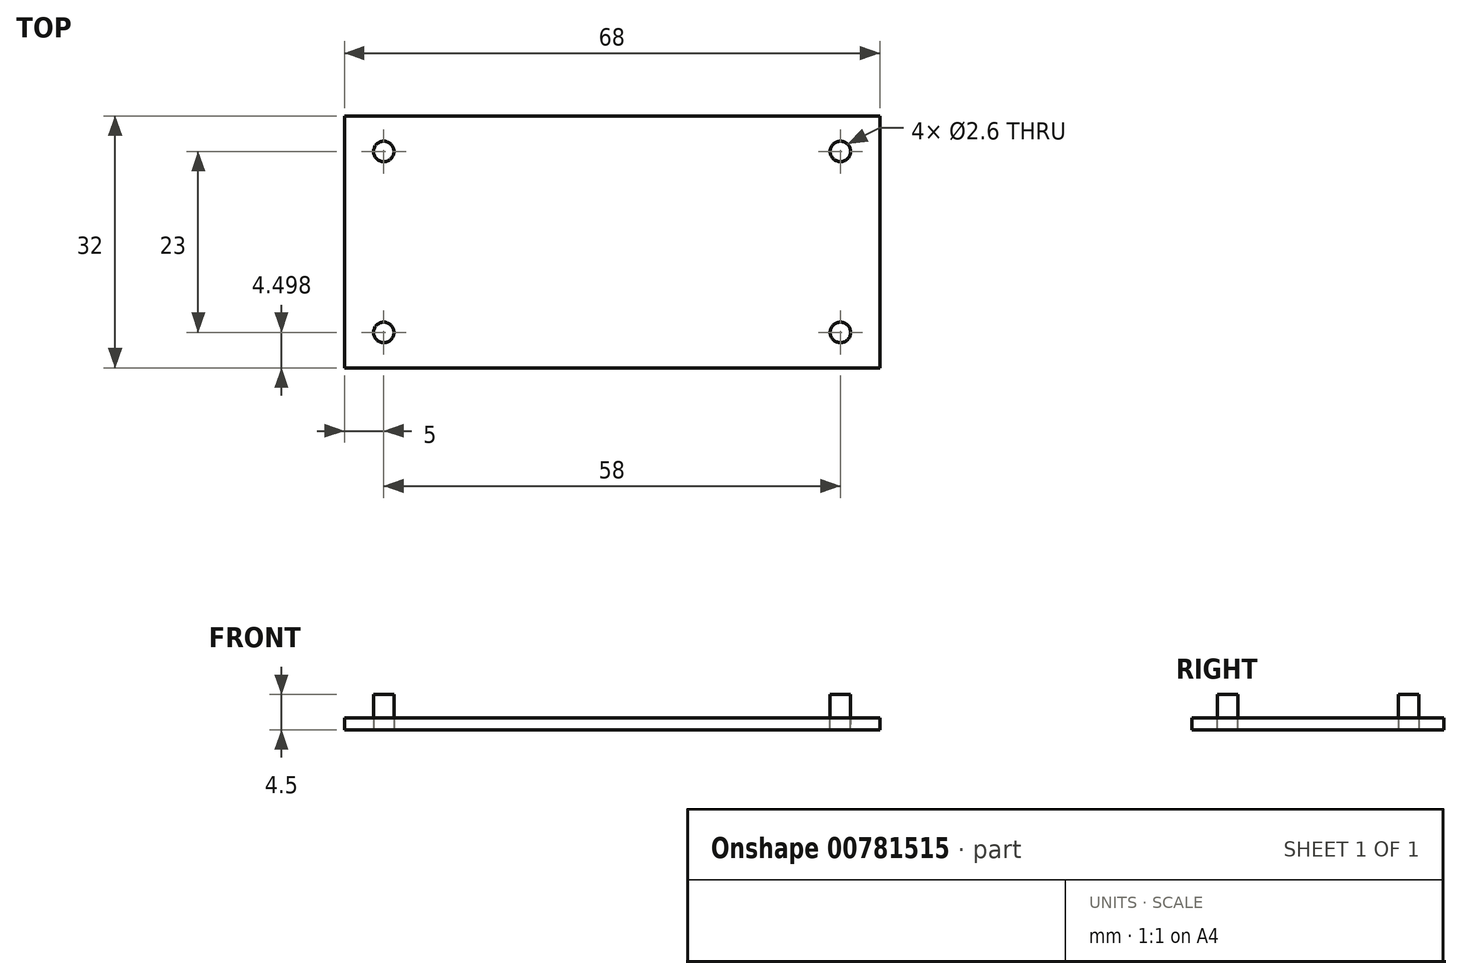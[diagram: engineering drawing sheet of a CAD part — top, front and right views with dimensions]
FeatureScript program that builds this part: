
annotation { "Feature Type Name" : "Feature", "Feature Type Description" : "" }
export const myFeature = defineFeature(function(context is Context, id is Id, definition is map)
    precondition{}
    {
        {
            var Q0;
            Q0=qCreatedBy(makeId("Top.planeOp"),FACE);
            var sketch = newSketch(context, id + "F0", { "sketchPlane" : qUnion([Q0])});
            skLineSegment(sketch, "E0.bottom", {"start": v(-34.03, 16) * mm, "end": v(33.97, 16) * mm});
            skLineSegment(sketch, "E0.top", {"start": v(-34.03, -16) * mm, "end": v(33.97, -16) * mm});
            skLineSegment(sketch, "E0.left", {"start": v(-34.03, 16) * mm, "end": v(-34.03, -16) * mm});
            skLineSegment(sketch, "E0.right", {"start": v(33.97, 16) * mm, "end": v(33.97, -16) * mm});
            skCircle(sketch, "E1", {"center": v(-29.03, 11.5) * mm, "radius": 1.3 * mm});
            skCircle(sketch, "E2", {"center": v(28.97, 11.5) * mm, "radius": 1.3 * mm});
            skCircle(sketch, "E3", {"center": v(28.97, -11.5) * mm, "radius": 1.3 * mm});
            skCircle(sketch, "E4", {"center": v(-29.03, -11.5) * mm, "radius": 1.3 * mm});
            skSolve(sketch);
        }
        {
            var Q0;
            Q0=makeQuery(id+"F0.imprint","IMPRINT",FACE,{"disambiguationData":[TD([[makeQuery(id+"F0.imprint","IMPRINT",EDGE,{"derivedFrom":sQuery(id+"F0.wireOp",EDGE,"E4")}),1.0]])]});
            var Q1;
            Q1=makeQuery(id+"F0.imprint","IMPRINT",FACE,{"disambiguationData":[TD([[makeQuery(id+"F0.imprint","IMPRINT",EDGE,{"derivedFrom":sQuery(id+"F0.wireOp",EDGE,"E1")}),1.0]])]});
            var Q2;
            Q2=makeQuery(id+"F0.imprint","IMPRINT",FACE,{"disambiguationData":[TD([[makeQuery(id+"F0.imprint","IMPRINT",EDGE,{"derivedFrom":sQuery(id+"F0.wireOp",EDGE,"E2")}),1.0]])]});
            var Q3;
            Q3=makeQuery(id+"F0.imprint","IMPRINT",FACE,{"disambiguationData":[TD([[makeQuery(id+"F0.imprint","IMPRINT",EDGE,{"derivedFrom":sQuery(id+"F0.wireOp",EDGE,"E3")}),1.0]])]});
            extrude(context, id + "F1", {"entities" : qUnion([Q0, Q1, Q2, Q3]), "depth" : 3 * mm, "offsetDistance" : 25 * mm, "hasSecondDirection" : true, "secondDirectionOppositeDirection" : true, "secondDirectionDepth" : 1.5 * mm});
        }
        {
            var Q0;
            Q0=qSketchRegion(id+"F0",true);
            extrude(context, id + "F2", {"entities" : qUnion([Q0]), "oppositeDirection" : true, "depth" : 1.5 * mm, "offsetDistance" : 25 * mm});
        }
    });
